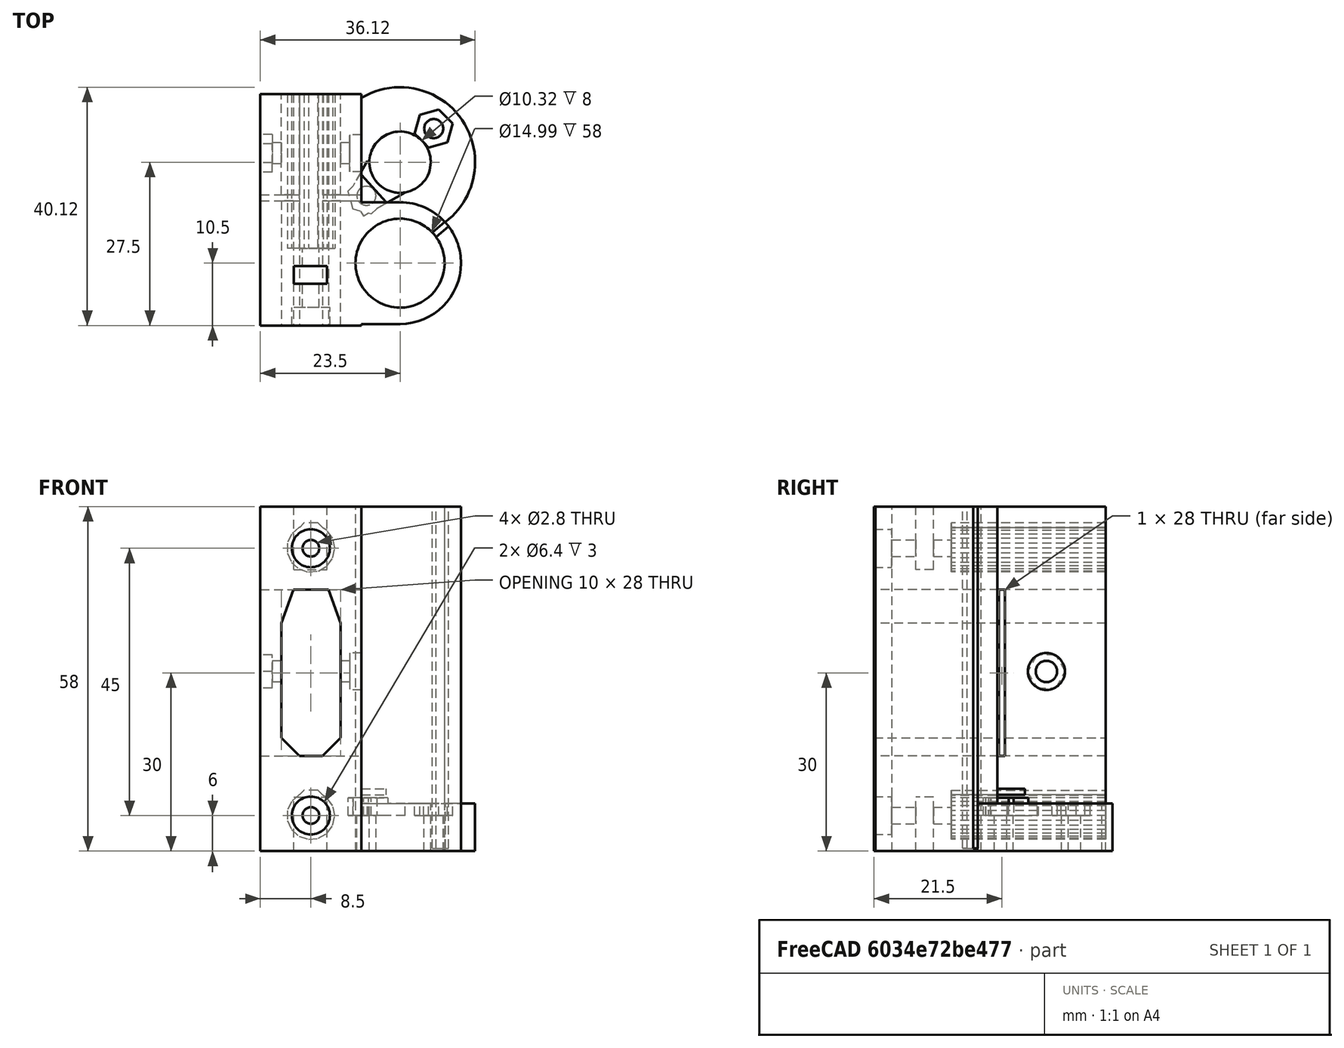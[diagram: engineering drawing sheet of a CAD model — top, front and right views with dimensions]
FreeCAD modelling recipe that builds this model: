
FCSTD DOCUMENT  (FreeCAD 0.19R)
Label: x-end-idler
License: All rights reserved
LicenseURL: http://en.wikipedia.org/wiki/All_rights_reserved
objects: Part::Box×18, Part::Cylinder×14, Part::Fuse×6, Part::MultiFuse×6, Part::Cut×5, Part::Prism×5, Part::Mirroring×1
note: 55 computed .brp shape members not serialized (recipe doc carries the construction recipe); baked Part::Feature solids carry a one-line shape summary decoded from their .brp

FEATURE [Part::Box] cube
  AttacherType = Attacher::AttachEngine3D
  Height = 58
  Length = 17
  Placement = pos=(-23.5,-28.5,0) rot=(0,0,1;0rad)
  Width = 39
FEATURE [Part::Box] cube001
  AttacherType = Attacher::AttachEngine3D
  Height = 58
  Length = 14.25
  Placement = pos=(-14.25,-10.25,0) rot=(0,0,1;0rad)
  Width = 20.5
FEATURE [Part::Cylinder] cylinder
  Angle = 360
  AttacherType = Attacher::AttachEngine3D
  Height = 58
  Radius = 10.25
FEATURE [Part::Fuse] Group
  Base = -> cube001
  Tool = -> cylinder
FEATURE [Part::Cylinder] cylinder001
  Angle = 360
  AttacherType = Attacher::AttachEngine3D
  Height = 8
  Placement = pos=(0,-17,0) rot=(0,0,1;0rad)
  Radius = 12.6247
FEATURE [Part::Box] cube002
  AttacherType = Attacher::AttachEngine3D
  Height = 1
  Length = 10
  Placement = pos=(-7.46897,-15.9937,9.5) rot=(0,0,1;0.841249rad)
  Width = 5
FEATURE [Part::MultiFuse] Group001
  Shapes = -> [cube,Group,cylinder001,cube002]
FEATURE [Part::Cylinder] cylinder002
  Angle = 360
  AttacherType = Attacher::AttachEngine3D
  Height = 62
  Placement = pos=(0,0,-1) rot=(0,0,1;0rad)
  Radius = 7.49334
FEATURE [Part::Box] cube003
  AttacherType = Attacher::AttachEngine3D
  Height = 62
  Length = 6
  Placement = pos=(3.0109,-3.17915,0.5) rot=(0,0,-1;0.698132rad)
  Width = 1
FEATURE [Part::Fuse] Group002
  Base = -> cylinder002
  Tool = -> cube003
FEATURE [Part::Box] cube004
  AttacherType = Attacher::AttachEngine3D
  Height = 28
  Length = 18
  Placement = pos=(-23,-11.5,16) rot=(0,0,1;0rad)
  Width = 1
FEATURE [Part::Box] cube005
  AttacherType = Attacher::AttachEngine3D
  Height = 28
  Length = 10
  Placement = pos=(-19,-42.5,16) rot=(0,0,1;0rad)
  Width = 65
FEATURE [Part::Box] cube006
  AttacherType = Attacher::AttachEngine3D
  Height = 28
  Length = 10
  Placement = pos=(-28.4867,-42.5,41.5544) rot=(0,1,0;0.349066rad)
  Width = 65
FEATURE [Part::Box] cube007
  AttacherType = Attacher::AttachEngine3D
  Height = 28
  Length = 10
  Placement = pos=(-8.91018,-42.5,38.1342) rot=(0,-1,0;0.349066rad)
  Width = 65
FEATURE [Part::Box] cube008
  AttacherType = Attacher::AttachEngine3D
  Height = 28
  Length = 10
  Placement = pos=(-27.435,-42.5,0.636039) rot=(0,1,0;0.785398rad)
  Width = 65
FEATURE [Part::Box] cube009
  AttacherType = Attacher::AttachEngine3D
  Height = 28
  Length = 10
  Placement = pos=(-7.63604,-42.5,-6.43503) rot=(0,-1,0;0.785398rad)
  Width = 65
FEATURE [Part::MultiFuse] union
  Shapes = -> [cube006,cube007,cube008,cube009]
FEATURE [Part::Cut] difference
  Base = -> cube005
  Tool = -> union
FEATURE [Part::Fuse] Matrix_Union
  Base = -> cube004
  Placement = pos=(-1,0,0) rot=(0,0,1;0rad)
  Tool = -> difference
FEATURE [Part::Prism] prism
  AttacherType = Attacher::AttachEngine3D
  Circumradius = 4.03601
  FirstAngle = 0
  Height = 50
  Polygon = 15
  SecondAngle = 0
FEATURE [Part::Box] cube010
  AttacherType = Attacher::AttachEngine3D
  Height = 50
  Length = 3.85
  Placement = pos=(2e-16,-5.42411,0) rot=(0,0,1;0.785398rad)
  Width = 3.85
FEATURE [Part::Box] cube011
  AttacherType = Attacher::AttachEngine3D
  Height = 50
  Length = 7.7
  Placement = pos=(-3.85,-8.1,0) rot=(0,0,1;0rad)
  Width = 3.85
FEATURE [Part::Cut] difference001
  Base = -> cube010
  Tool = -> cube011
FEATURE [Part::Fuse] Group003
  Base = -> prism
  Placement = pos=(-15,-41.5,6) rot=(-1,0,0;1.5708rad)
  Tool = -> difference001
FEATURE [Part::Prism] prism001
  AttacherType = Attacher::AttachEngine3D
  Circumradius = 4.03601
  FirstAngle = 0
  Height = 50
  Polygon = 15
  SecondAngle = 0
FEATURE [Part::Box] cube012
  AttacherType = Attacher::AttachEngine3D
  Height = 50
  Length = 3.85
  Placement = pos=(2e-16,-5.42411,0) rot=(0,0,1;0.785398rad)
  Width = 3.85
FEATURE [Part::Box] cube013
  AttacherType = Attacher::AttachEngine3D
  Height = 50
  Length = 7.7
  Placement = pos=(-3.85,-8.1,0) rot=(0,0,1;0rad)
  Width = 3.85
FEATURE [Part::Cut] difference002
  Base = -> cube012
  Tool = -> cube013
FEATURE [Part::Fuse] Group004
  Base = -> prism001
  Placement = pos=(-15,-41.5,51) rot=(-1,0,0;1.5708rad)
  Tool = -> difference002
FEATURE [Part::Cylinder] cylinder003
  Angle = 360
  AttacherType = Attacher::AttachEngine3D
  Height = 9.01
  Placement = pos=(0,-17,-1) rot=(0,0,1;0rad)
  Radius = 5.16233
FEATURE [Part::Cylinder] cylinder004
  Angle = 360
  AttacherType = Attacher::AttachEngine3D
  Height = 10
  Placement = pos=(5.65685,-22.6569,-1) rot=(0,0,1;3.92699rad)
  Radius = 1.6
FEATURE [Part::Cylinder] cylinder005
  Angle = 360
  AttacherType = Attacher::AttachEngine3D
  Height = 10
  Placement = pos=(-5.65685,-11.3431,-1) rot=(0,0,1;3.92699rad)
  Radius = 1.6
FEATURE [Part::Prism] prism002
  AttacherType = Attacher::AttachEngine3D
  Circumradius = 3.3
  FirstAngle = 0
  Height = 3
  Placement = pos=(5.65685,-22.6569,6) rot=(0,0,1;3.92699rad)
  Polygon = 6
  SecondAngle = 0
FEATURE [Part::Prism] prism003
  AttacherType = Attacher::AttachEngine3D
  Circumradius = 3.2
  FirstAngle = 0
  Height = 3
  Placement = pos=(-5.65685,-11.3431,6) rot=(0,0,1;4.45059rad)
  Polygon = 6
  SecondAngle = 0
FEATURE [Part::Box] cube014
  AttacherType = Attacher::AttachEngine3D
  Height = 3
  Length = 5
  Placement = pos=(-5.5,-17.2,6) rot=(0,0,1;0.523599rad)
  Width = 5
FEATURE [Part::Box] cube015
  AttacherType = Attacher::AttachEngine3D
  Height = 3
  Length = 5
  Placement = pos=(0,-17.2,6) rot=(0,0,1;1.0472rad)
  Width = 10
FEATURE [Part::MultiFuse] Group005
  Shapes = -> [Group002,Matrix_Union,Group003,Group004,cylinder003,cylinder004,cylinder005,prism002,prism003,cube014,cube015]
FEATURE [Part::Cylinder] cylinder006
  Angle = 360
  AttacherType = Attacher::AttachEngine3D
  Height = 80
  Placement = pos=(0,-22,30.25) rot=(0,-1,0;1.5708rad)
  Radius = 1.8
FEATURE [Part::Cylinder] cylinder007
  Angle = 360
  AttacherType = Attacher::AttachEngine3D
  Height = 10
  Placement = pos=(1.5,-22,30.25) rot=(0,-1,0;1.5708rad)
  Radius = 3.1
FEATURE [Part::Prism] prism004
  AttacherType = Attacher::AttachEngine3D
  Circumradius = 3.2
  FirstAngle = 0
  Height = 80
  Placement = pos=(-21.5,-22,30.25) rot=(-0.250563,-0.935113,0.250563;1.63783rad)
  Polygon = 6
  SecondAngle = 0
FEATURE [Part::MultiFuse] Matrix_Union001
  Placement = pos=(0,3.5,0) rot=(0,0,1;0rad)
  Shapes = -> [cylinder006,cylinder007,prism004]
FEATURE [Part::Fuse] Group006
  Base = -> Group005
  Tool = -> Matrix_Union001
FEATURE [Part::Cut] difference003
  Base = -> Group001
  Tool = -> Group006
FEATURE [Part::Cylinder] cylinder008
  Angle = 360
  AttacherType = Attacher::AttachEngine3D
  Height = 11
  Placement = pos=(-15,8.5,6) rot=(1,0,0;1.5708rad)
  Radius = 6
FEATURE [Part::Cylinder] cylinder009
  Angle = 360
  AttacherType = Attacher::AttachEngine3D
  Height = 11
  Placement = pos=(-15,8.5,51) rot=(1,0,0;1.5708rad)
  Radius = 6
FEATURE [Part::MultiFuse] union001
  Shapes = -> [difference003,cylinder008,cylinder009]
FEATURE [Part::Cylinder] cylinder010
  Angle = 360
  AttacherType = Attacher::AttachEngine3D
  Height = 12
  Placement = pos=(-15,8.5,6) rot=(1,0,0;1.5708rad)
  Radius = 1.4
FEATURE [Part::Cylinder] cylinder011
  Angle = 360
  AttacherType = Attacher::AttachEngine3D
  Height = 12
  Placement = pos=(-15,8.5,51) rot=(1,0,0;1.5708rad)
  Radius = 1.4
FEATURE [Part::Cylinder] cylinder012
  Angle = 360
  AttacherType = Attacher::AttachEngine3D
  Height = 4
  Placement = pos=(-15,11.5,6) rot=(1,0,0;1.5708rad)
  Radius = 3.2
FEATURE [Part::Cylinder] cylinder013
  Angle = 360
  AttacherType = Attacher::AttachEngine3D
  Height = 4
  Placement = pos=(-15,11.5,51) rot=(1,0,0;1.5708rad)
  Radius = 3.2
FEATURE [Part::Box] cube016
  AttacherType = Attacher::AttachEngine3D
  Height = 20
  Length = 5.6
  Placement = pos=(-17.9,0.5,47.4) rot=(0,0,1;0rad)
  Width = 3
FEATURE [Part::Box] cube017
  AttacherType = Attacher::AttachEngine3D
  Height = 16
  Length = 5.6
  Placement = pos=(-17.9,0.5,-6.9) rot=(0,0,1;0rad)
  Width = 3
FEATURE [Part::MultiFuse] Group007
  Shapes = -> [cylinder010,cylinder011,cylinder012,cylinder013,cube016,cube017]
FEATURE [Part::Cut] difference004
  Base = -> union001
  Refine = true
  Tool = -> Group007
FEATURE [Part::Mirroring] mirr_difference004  label="mirrored difference004"
  Base = (0,0,0)
  Normal = (0,1,0)
  Source = -> difference004
